# Revit family: Arper_Aava-02_trestle-swivel_polypropylene_7603
name_source: partatom
category: Furniture
units: mm (PartAtom-declared; Revit-internal decimal feet)

## family parameters
Always vertical = Yes
Cut with Voids When Loaded = No
OmniClass Number = 23.40.20.00
OmniClass Title = General Furniture and Specialties
Room Calculation Point = No
Shared = No
Work Plane-Based = No

## types (1)
- Arper_Aava-02_trestle-swivel_polypropylene_7603
    Default Elevation = 0 mm  [stored 0 ft]
    Description = Chair on a swivel trestle base in powder-coated aluminium. Shell in 
polypropylene made with post-consumer recycled materials, mixed 
with virgin material, available in 5 colours. Optional armrests in the 
same colour as the base are also available, equipped with pads in 
polypropylene in the same finish of the shell. Glides are also 
available, with felt insert for wood floors.
    Manufacturer = ARPER s.p.a.
    Model = Aava 02
    URL = http://www.arper.com

note: [stored X ft] marks values corroborated as IEEE doubles in the binary element streams (Revit-internal decimal feet)
